# Revit family: Storage-Teknion-MXCRV-Elevated_Credenza_Ventilated_And_Integrated_Fridge-Expansion_Meeting-R2023
name_source: partatom
category: Furniture
units: mm (PartAtom-declared; Revit-internal decimal feet)

## family parameters
Always vertical = Yes
Cut with Voids When Loaded = No
Enable Cutting in Views = No
OmniClass Number = 23.40.20.00
OmniClass Title = General Furniture and Specialties
Render Appearance Source = Family Geometry
Room Calculation Point = No
Shared = Yes
Work Plane-Based = No

## types (6) — shared parameters
Assembly Code = E2020200
Manufacturer = Teknion
Manufacturer Fax = 416.661.4586
Part Number = MXCRV
Product Documentation Link = http://www.teknion.com
Product Line = Credenzas
Product Page URL = http://www.teknion.com
Series = Meeting Expansion
Sustainability Data = https://www.teknion.com
URL = www.teknion.com
Unit Weight URL = http://www.teknion.com
Warranty = http://www.teknion.com
zero-valued in all types: Default Elevation

## per-type parameters (varying)
| type | 1 Pull-Out Bin | 2 Pull-Out Bins | Blade Foot | Description | Model | No Pull-Out Bin | Square Foot |
| No Pull-Out Bin / Square Foot | No | No | No | Meeting Expansion, Elevated Credenza – Ventilated & Integrated Fridge - No Pull-Out Bin | MXCRVS24__36_N | Yes | Yes |
| 1 Pull-Out Bin / Blade Foot | Yes | No | Yes | Meeting Expansion, Elevated Credenza – Ventilated & Integrated Fridge - 1 Pull-Out Bin | MXCRVB24__36_1 | No | No |
| 2 Pull-Out Bins / Square Foot | No | Yes | No | Meeting Expansion, Elevated Credenza – Ventilated & Integrated Fridge - 2 Pull-Out Bins | MXCRVS24__36_2 | No | Yes |
| 2 Pull-Out Bins / Blade Foot | No | Yes | Yes | Meeting Expansion, Elevated Credenza – Ventilated & Integrated Fridge - 2 Pull-Out Bins | MXCRVB24__36_2 | No | No |
| 1 Pull-Out Bin / Square Foot | Yes | No | No | Meeting Expansion, Elevated Credenza – Ventilated & Integrated Fridge - 1 Pull-Out Bin | MXCRVS24__36_1 | No | Yes |
| No Pull-Out Bin / Blade Foot | No | No | Yes | Meeting Expansion, Elevated Credenza – Ventilated & Integrated Fridge - No Pull-Out Bin | MXCRVB24__36_N | Yes | No |

## geometry (parser evidence)
native form markers: Sweep x4
no freeform markers — native parametric forms only
